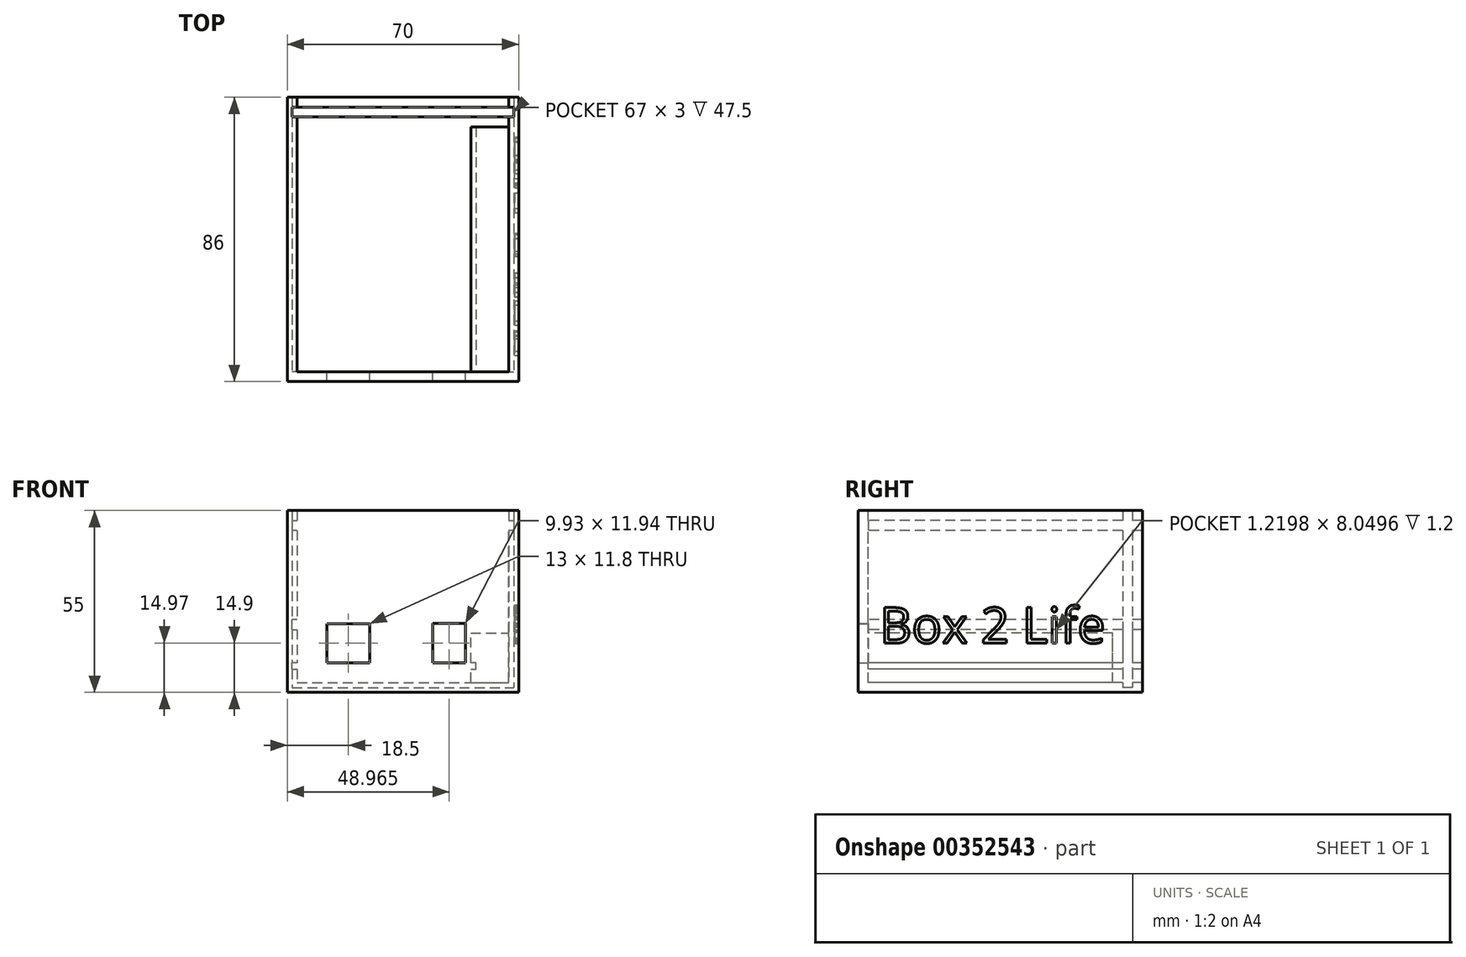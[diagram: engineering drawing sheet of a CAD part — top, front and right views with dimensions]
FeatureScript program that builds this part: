
annotation { "Feature Type Name" : "Feature", "Feature Type Description" : "" }
export const myFeature = defineFeature(function(context is Context, id is Id, definition is map)
    precondition{}
    {
        {
            var Q0;
            Q0=qCreatedBy(makeId("Front.planeOp"),FACE);
            var sketch = newSketch(context, id + "F0", { "sketchPlane" : qUnion([Q0])});
            skLineSegment(sketch, "E0.bottom", {"start": v(0, 0) * mm, "end": v(70, 0) * mm});
            skLineSegment(sketch, "E0.left", {"start": v(0, 0) * mm, "end": v(0, 55) * mm});
            skLineSegment(sketch, "E0.right", {"start": v(70, 0) * mm, "end": v(70, 55) * mm});
            skLineSegment(sketch, "E1.bottom", {"start": v(12.5, 20.3) * mm, "end": v(24.5, 20.3) * mm, "construction": true});
            skLineSegment(sketch, "E1.top", {"start": v(12.5, 9.5) * mm, "end": v(24.5, 9.5) * mm, "construction": true});
            skLineSegment(sketch, "E1.left", {"start": v(12.5, 20.3) * mm, "end": v(12.5, 9.5) * mm, "construction": true});
            skLineSegment(sketch, "E1.right", {"start": v(24.5, 20.3) * mm, "end": v(24.5, 9.5) * mm, "construction": true});
            skLineSegment(sketch, "E2.bottom", {"start": v(44.5, 20.44) * mm, "end": v(53.43, 20.44) * mm, "construction": true});
            skLineSegment(sketch, "E2.top", {"start": v(44.5, 9.5) * mm, "end": v(53.43, 9.5) * mm, "construction": true});
            skLineSegment(sketch, "E2.left", {"start": v(44.5, 20.44) * mm, "end": v(44.5, 9.5) * mm, "construction": true});
            skLineSegment(sketch, "E2.right", {"start": v(53.43, 20.44) * mm, "end": v(53.43, 9.5) * mm, "construction": true});
            skLineSegment(sketch, "E3.0", {"start": v(12, 20.8) * mm, "end": v(25, 20.8) * mm});
            skLineSegment(sketch, "E3.1", {"start": v(12, 20.8) * mm, "end": v(12, 9) * mm});
            skLineSegment(sketch, "E3.2", {"start": v(12, 9) * mm, "end": v(25, 9) * mm});
            skLineSegment(sketch, "E3.3", {"start": v(25, 20.8) * mm, "end": v(25, 9) * mm});
            skLineSegment(sketch, "E4.0", {"start": v(44, 20.94) * mm, "end": v(53.93, 20.94) * mm});
            skLineSegment(sketch, "E4.1", {"start": v(44, 20.94) * mm, "end": v(44, 9) * mm});
            skLineSegment(sketch, "E4.2", {"start": v(44, 9) * mm, "end": v(53.93, 9) * mm});
            skLineSegment(sketch, "E4.3", {"start": v(53.93, 20.94) * mm, "end": v(53.93, 9) * mm});
            skLineSegment(sketch, "E5.0", {"start": v(3, 3) * mm, "end": v(3, 7) * mm});
            skLineSegment(sketch, "E5.1", {"start": v(3, 3) * mm, "end": v(55.54, 3) * mm});
            skLineSegment(sketch, "E6", {"start": v(3, 7) * mm, "end": v(1.5, 7) * mm});
            skLineSegment(sketch, "E7", {"start": v(1.5, 7) * mm, "end": v(1.5, 9) * mm});
            skLineSegment(sketch, "E8", {"start": v(1.5, 9) * mm, "end": v(3, 9) * mm});
            skLineSegment(sketch, "E9", {"start": v(55.54, 3) * mm, "end": v(55.54, 7) * mm});
            skLineSegment(sketch, "E10", {"start": v(55.54, 7) * mm, "end": v(57.04, 7) * mm});
            skLineSegment(sketch, "E11", {"start": v(57.04, 7) * mm, "end": v(57.04, 9) * mm});
            skLineSegment(sketch, "E12", {"start": v(57.04, 9) * mm, "end": v(55.54, 9) * mm});
            skLineSegment(sketch, "E13", {"start": v(55.54, 9) * mm, "end": v(55.54, 18) * mm});
            skLineSegment(sketch, "E14", {"start": v(55.54, 18) * mm, "end": v(67, 18) * mm});
            skLineSegment(sketch, "E15", {"start": v(3, 9) * mm, "end": v(3, 19) * mm});
            skLineSegment(sketch, "E16", {"start": v(67, 18) * mm, "end": v(67, 49) * mm});
            skLineSegment(sketch, "E17", {"start": v(67, 55) * mm, "end": v(70, 55) * mm});
            skLineSegment(sketch, "E18", {"start": v(0, 55) * mm, "end": v(3, 55) * mm});
            skLineSegment(sketch, "E19", {"start": v(3, 52) * mm, "end": v(1.5, 52) * mm});
            skLineSegment(sketch, "E20", {"start": v(1.5, 52) * mm, "end": v(1.5, 49) * mm});
            skLineSegment(sketch, "E21", {"start": v(1.5, 49) * mm, "end": v(3, 49) * mm});
            skLineSegment(sketch, "E22.trimOffspring", {"start": v(3, 52) * mm, "end": v(3, 55) * mm});
            skLineSegment(sketch, "E23", {"start": v(67, 52) * mm, "end": v(68.5, 52) * mm});
            skLineSegment(sketch, "E24", {"start": v(68.5, 52) * mm, "end": v(68.5, 49) * mm});
            skLineSegment(sketch, "E25", {"start": v(68.5, 49) * mm, "end": v(67, 49) * mm});
            skLineSegment(sketch, "E26.trimOffspring", {"start": v(67, 52) * mm, "end": v(67, 55) * mm});
            skLineSegment(sketch, "E27", {"start": v(0, 55) * mm, "end": v(70, 55) * mm, "construction": true});
            skLineSegment(sketch, "E28", {"start": v(55.54, 3) * mm, "end": v(67, 3) * mm, "construction": true});
            skLineSegment(sketch, "E29", {"start": v(67, 3) * mm, "end": v(67, 18) * mm, "construction": true});
            skLineSegment(sketch, "E30", {"start": v(3, 19) * mm, "end": v(1.5, 19) * mm});
            skLineSegment(sketch, "E31", {"start": v(1.5, 19) * mm, "end": v(1.5, 22) * mm});
            skLineSegment(sketch, "E32", {"start": v(1.5, 22) * mm, "end": v(3, 22) * mm});
            skLineSegment(sketch, "E33.trimOffspring", {"start": v(3, 22) * mm, "end": v(3, 49) * mm});
            skSolve(sketch);
        }
        {
            var Q0;
            Q0=makeQuery(id+"F0.imprint","IMPRINT",FACE,{"disambiguationData":[TD([[makeQuery(id+"F0.imprint","IMPRINT",EDGE,{"derivedFrom":sQuery(id+"F0.wireOp",EDGE,"E0.bottom")}),1.0]])]});
            extrude(context, id + "F1", {"entities" : qUnion([Q0]), "oppositeDirection" : true, "depth" : 74 * mm});
        }
        {
            var Q0;
            Q0=makeQuery(id+"F0.imprint","IMPRINT",FACE,{"disambiguationData":[TD([[makeQuery(id+"F0.imprint","IMPRINT",EDGE,{"derivedFrom":sQuery(id+"F0.wireOp",EDGE,"E0.bottom")}),1.0]])]});
            var sketch = newSketch(context, id + "F2", { "sketchPlane" : qUnion([Q0])});
            skLineSegment(sketch, "E34.0", {"start": v(0, 0) * mm, "end": v(0, 55) * mm});
            skLineSegment(sketch, "E35.0", {"start": v(0, 0) * mm, "end": v(70, 0) * mm});
            skLineSegment(sketch, "E36.0", {"start": v(70, 0) * mm, "end": v(70, 55) * mm});
            skLineSegment(sketch, "E37.0", {"start": v(0, 55) * mm, "end": v(70, 55) * mm});
            skLineSegment(sketch, "E38.0", {"start": v(12, 20.8) * mm, "end": v(25, 20.8) * mm});
            skLineSegment(sketch, "E39.0", {"start": v(12, 20.8) * mm, "end": v(12, 9) * mm});
            skLineSegment(sketch, "E40.0", {"start": v(12, 9) * mm, "end": v(25, 9) * mm});
            skLineSegment(sketch, "E41.0", {"start": v(25, 20.8) * mm, "end": v(25, 9) * mm});
            skLineSegment(sketch, "E42.0", {"start": v(44, 20.94) * mm, "end": v(44, 9) * mm});
            skLineSegment(sketch, "E43.0", {"start": v(44, 20.94) * mm, "end": v(53.93, 20.94) * mm});
            skLineSegment(sketch, "E44.0", {"start": v(53.93, 20.94) * mm, "end": v(53.93, 9) * mm});
            skLineSegment(sketch, "E45.0", {"start": v(44, 9) * mm, "end": v(53.93, 9) * mm});
            skSolve(sketch);
        }
        {
            var Q0;
            Q0=qSketchRegion(id+"F2",true);
            extrude(context, id + "F3", {"entities" : qUnion([Q0]), "operationType" : NewBodyOperationType.ADD, "depth" : 3 * mm});
        }
        {
            var Q0;
            Q0=makeQuery(id+"F1.opExtrude","CAP_FACE",FACE,{"disambiguationData":[OSD([sQuery(id+"F0.wireOp",EDGE,"E0.bottom"),sQuery(id+"F0.wireOp",EDGE,"E0.left"),sQuery(id+"F0.wireOp",EDGE,"E0.right"),sQuery(id+"F0.wireOp",EDGE,"E5.0"),sQuery(id+"F0.wireOp",EDGE,"E5.1"),sQuery(id+"F0.wireOp",EDGE,"E6"),sQuery(id+"F0.wireOp",EDGE,"E7"),sQuery(id+"F0.wireOp",EDGE,"E8"),sQuery(id+"F0.wireOp",EDGE,"E9"),sQuery(id+"F0.wireOp",EDGE,"E10"),sQuery(id+"F0.wireOp",EDGE,"E11"),sQuery(id+"F0.wireOp",EDGE,"E12"),sQuery(id+"F0.wireOp",EDGE,"E13"),sQuery(id+"F0.wireOp",EDGE,"E14"),sQuery(id+"F0.wireOp",EDGE,"E15"),sQuery(id+"F0.wireOp",EDGE,"E16"),sQuery(id+"F0.wireOp",EDGE,"E17"),sQuery(id+"F0.wireOp",EDGE,"E18"),sQuery(id+"F0.wireOp",EDGE,"E19"),sQuery(id+"F0.wireOp",EDGE,"E20"),sQuery(id+"F0.wireOp",EDGE,"E21"),sQuery(id+"F0.wireOp",EDGE,"E22.trimOffspring"),sQuery(id+"F0.wireOp",EDGE,"E23"),sQuery(id+"F0.wireOp",EDGE,"E24"),sQuery(id+"F0.wireOp",EDGE,"E25"),sQuery(id+"F0.wireOp",EDGE,"E26.trimOffspring")])],"isStart":false});
            var sketch = newSketch(context, id + "F4", { "sketchPlane" : qUnion([Q0])});
            skLineSegment(sketch, "E46.0", {"start": v(-70, 0) * mm, "end": v(-70, 55) * mm});
            skLineSegment(sketch, "E47.0", {"start": v(-67, 55) * mm, "end": v(-70, 55) * mm});
            skLineSegment(sketch, "E48.0", {"start": v(-67, 52) * mm, "end": v(-67, 55) * mm});
            skLineSegment(sketch, "E49.0", {"start": v(-67, 52) * mm, "end": v(-68.5, 52) * mm});
            skLineSegment(sketch, "E50.0", {"start": v(-68.5, 52) * mm, "end": v(-68.5, 49) * mm});
            skLineSegment(sketch, "E51.0", {"start": v(-68.5, 49) * mm, "end": v(-67, 49) * mm});
            skLineSegment(sketch, "E52.0", {"start": v(-67, 18) * mm, "end": v(-67, 49) * mm});
            skLineSegment(sketch, "E53.0", {"start": v(-67, 3) * mm, "end": v(-67, 18) * mm});
            skLineSegment(sketch, "E54.0", {"start": v(-55.54, 3) * mm, "end": v(-67, 3) * mm});
            skLineSegment(sketch, "E55.0", {"start": v(-3, 3) * mm, "end": v(-55.54, 3) * mm});
            skLineSegment(sketch, "E56.0", {"start": v(-3, 3) * mm, "end": v(-3, 7) * mm});
            skLineSegment(sketch, "E57.0", {"start": v(-3, 7) * mm, "end": v(-1.5, 7) * mm});
            skLineSegment(sketch, "E58.0", {"start": v(-1.5, 7) * mm, "end": v(-1.5, 9) * mm});
            skLineSegment(sketch, "E59.0", {"start": v(-1.5, 9) * mm, "end": v(-3, 9) * mm});
            skLineSegment(sketch, "E60.0", {"start": v(-3, 9) * mm, "end": v(-3, 19) * mm});
            skLineSegment(sketch, "E61.0", {"start": v(-1.5, 49) * mm, "end": v(-3, 49) * mm});
            skLineSegment(sketch, "E62.0", {"start": v(-1.5, 52) * mm, "end": v(-1.5, 49) * mm});
            skLineSegment(sketch, "E63.0", {"start": v(-3, 52) * mm, "end": v(-1.5, 52) * mm});
            skLineSegment(sketch, "E64.0", {"start": v(-3, 52) * mm, "end": v(-3, 55) * mm});
            skLineSegment(sketch, "E65.0", {"start": v(0, 55) * mm, "end": v(-3, 55) * mm});
            skLineSegment(sketch, "E66.0", {"start": v(0, 0) * mm, "end": v(0, 55) * mm});
            skLineSegment(sketch, "E67.0", {"start": v(0, 0) * mm, "end": v(-70, 0) * mm});
            skLineSegment(sketch, "E68", {"start": v(-3, 19) * mm, "end": v(-1.5, 19) * mm});
            skLineSegment(sketch, "E69", {"start": v(-1.5, 19) * mm, "end": v(-1.5, 22) * mm});
            skLineSegment(sketch, "E70", {"start": v(-1.5, 22) * mm, "end": v(-3, 22) * mm});
            skLineSegment(sketch, "E71", {"start": v(-3, 22) * mm, "end": v(-3, 49) * mm});
            skSolve(sketch);
        }
        {
            var Q0;
            Q0=qSketchRegion(id+"F4",true);
            extrude(context, id + "F5", {"entities" : qUnion([Q0]), "operationType" : NewBodyOperationType.ADD, "depth" : 9 * mm});
        }
        {
            var Q0;
            Q0=makeQuery(id+"F5.boolean.opBoolean","MERGE",FACE,{"derivedFrom":[makeQuery(id+"F1.opExtrude","SWEPT_FACE",FACE,{"disambiguationData":[OSD([sQuery(id+"F0.wireOp",EDGE,"E16")])]}),makeQuery(id+"F5.opExtrude","SWEPT_FACE",FACE,{"disambiguationData":[OSD([sQuery(id+"F4.wireOp",EDGE,"E52.0"),sQuery(id+"F4.wireOp",EDGE,"E53.0")])]})]});
            cPlane(context, id + "F6", {"entities" : qUnion([Q0]), "cplaneType" : CPlaneType.OFFSET, "offset" : 0 * mm, "width" : 150 * mm, "height" : 150 * mm});
        }
        {
            var Q0;
            Q0=qCreatedBy(id+"F6.planeOp",FACE);
            var sketch = newSketch(context, id + "F7", { "sketchPlane" : qUnion([Q0])});
            skLineSegment(sketch, "E72.0", {"start": v(-83, 0) * mm, "end": v(-83, 55) * mm, "construction": true});
            skLineSegment(sketch, "E73", {"start": v(-83, 55) * mm, "end": v(-80, 55) * mm, "construction": true});
            skLineSegment(sketch, "E74", {"start": v(-80, 55) * mm, "end": v(-80, 3) * mm});
            skLineSegment(sketch, "E75", {"start": v(-77, 55) * mm, "end": v(-77, 3) * mm});
            skLineSegment(sketch, "E76", {"start": v(-77, 55) * mm, "end": v(-80, 55) * mm});
            skLineSegment(sketch, "E77", {"start": v(-80, 3) * mm, "end": v(-77, 3) * mm});
            skSolve(sketch);
        }
        {
            var Q0;
            Q0=qSketchRegion(id+"F7",true);
            extrude(context, id + "F8", {"entities" : qUnion([Q0]), "operationType" : NewBodyOperationType.REMOVE, "oppositeDirection" : true, "depth" : 1.5 * mm});
        }
        {
            var Q0;
            Q0=makeQuery(id+"F5.boolean.opBoolean","MERGE",FACE,{"derivedFrom":[makeQuery(id+"F1.opExtrude","SWEPT_FACE",FACE,{"disambiguationData":[OSD([sQuery(id+"F0.wireOp",EDGE,"E15")])]}),makeQuery(id+"F5.opExtrude","SWEPT_FACE",FACE,{"disambiguationData":[OSD([sQuery(id+"F4.wireOp",EDGE,"E60.0")])]})]});
            cPlane(context, id + "F9", {"entities" : qUnion([Q0]), "cplaneType" : CPlaneType.OFFSET, "offset" : 0 * mm, "width" : 150 * mm, "height" : 150 * mm});
        }
        {
            var Q0;
            Q0=qCreatedBy(id+"F9.planeOp",FACE);
            var sketch = newSketch(context, id + "F10", { "sketchPlane" : qUnion([Q0])});
            skPoint(sketch, "E78.0", {"position": v(77, 55) * mm});
            skLineSegment(sketch, "E79.bottom", {"start": v(77, 55) * mm, "end": v(80, 55) * mm});
            skLineSegment(sketch, "E79.left", {"start": v(77, 55) * mm, "end": v(77, 3) * mm});
            skLineSegment(sketch, "E80", {"start": v(80, 55) * mm, "end": v(80, 3) * mm});
            skLineSegment(sketch, "E81", {"start": v(80, 3) * mm, "end": v(77, 3) * mm});
            skSolve(sketch);
        }
        {
            var Q0;
            Q0=qSketchRegion(id+"F10",true);
            extrude(context, id + "F11", {"entities" : qUnion([Q0]), "operationType" : NewBodyOperationType.REMOVE, "oppositeDirection" : true, "depth" : 1.5 * mm});
        }
        {
            var Q0;
            Q0=makeQuery(id+"F5.boolean.opBoolean","MERGE",FACE,{"derivedFrom":[makeQuery(id+"F1.opExtrude","SWEPT_FACE",FACE,{"disambiguationData":[OSD([sQuery(id+"F0.wireOp",EDGE,"E5.1")])]}),makeQuery(id+"F5.opExtrude","SWEPT_FACE",FACE,{"disambiguationData":[OSD([sQuery(id+"F4.wireOp",EDGE,"E54.0"),sQuery(id+"F4.wireOp",EDGE,"E55.0")])]})]});
            var sketch = newSketch(context, id + "F12", { "sketchPlane" : qUnion([Q0])});
            skLineSegment(sketch, "E82.bottom", {"start": v(1.5, 80) * mm, "end": v(68.5, 80) * mm});
            skLineSegment(sketch, "E82.top", {"start": v(1.5, 77) * mm, "end": v(68.5, 77) * mm});
            skLineSegment(sketch, "E82.left", {"start": v(1.5, 80) * mm, "end": v(1.5, 77) * mm});
            skLineSegment(sketch, "E82.right", {"start": v(68.5, 80) * mm, "end": v(68.5, 77) * mm});
            skSolve(sketch);
        }
        {
            var Q0;
            Q0 = qSketchRegion(id + "F12", true);
            extrude(context, id + "F13", {"entities" : qUnion([Q0]), "operationType" : NewBodyOperationType.REMOVE, "oppositeDirection" : true, "depth" : 1.5 * mm});
        }
        {
            var Q0;
            Q0=makeQuery(id+"F5.boolean.opBoolean","MERGE",FACE,{"derivedFrom":[makeQuery(id+"F3.boolean.opBoolean","MERGE",FACE,{"derivedFrom":[makeQuery(id+"F1.opExtrude","SWEPT_FACE",FACE,{"disambiguationData":[OSD([sQuery(id+"F0.wireOp",EDGE,"E0.right")])]}),makeQuery(id+"F3.opExtrude","SWEPT_FACE",FACE,{"disambiguationData":[OSD([sQuery(id+"F2.wireOp",EDGE,"E36.0")])]})]}),makeQuery(id+"F5.opExtrude","SWEPT_FACE",FACE,{"disambiguationData":[OSD([sQuery(id+"F4.wireOp",EDGE,"E46.0")])]})]});
            var sketch = newSketch(context, id + "F14", { "sketchPlane" : qUnion([Q0])});
            skText(sketch, "E83", { "text": "Box 2 Life", "fontName": "OpenSans-Regular.ttf"});
            const initialGuessF14  = {"E83": [0.00348, 0.01492, 1, 0, 0.01083]};
            skSetInitialGuess(sketch, initialGuessF14);
            skSolve(sketch);
        }
        {
            var Q0;
            Q0=qSketchRegion(id+"F14",true);
            var Q1;
            Q1=qConstructionFilter(qBodyType(qCreatedBy(id+"F14",EDGE),BodyType.WIRE),ConstructionObject.NO);
            extrude(context, id + "F15", {"entities" : qUnion([Q0]), "operationType" : NewBodyOperationType.REMOVE, "surfaceEntities" : qUnion([Q1]), "oppositeDirection" : true, "depth" : 1.2 * mm});
        }
    });
